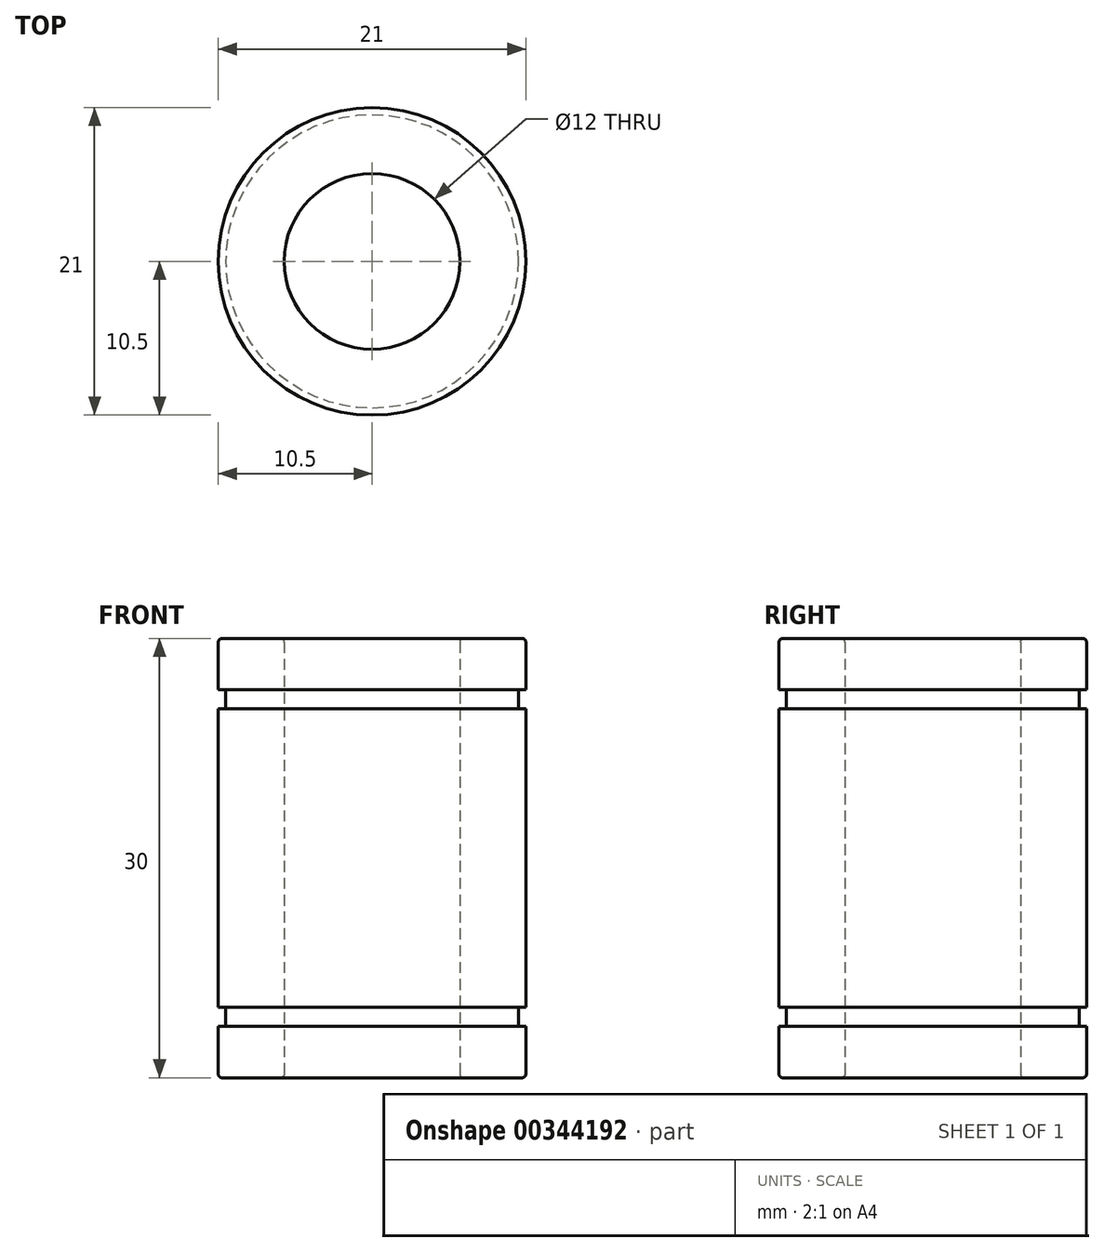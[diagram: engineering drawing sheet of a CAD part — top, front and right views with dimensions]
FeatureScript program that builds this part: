
annotation { "Feature Type Name" : "Feature", "Feature Type Description" : "" }
export const myFeature = defineFeature(function(context is Context, id is Id, definition is map)
    precondition{}
    {
        {
            var Q0;
            Q0=qCreatedBy(makeId("Top.planeOp"),FACE);
            var sketch = newSketch(context, id + "F0", { "sketchPlane" : qUnion([Q0])});
            skCircle(sketch, "E0", {"center": v(0, 0) * mm, "radius": 6 * mm});
            skCircle(sketch, "E1", {"center": v(0, 0) * mm, "radius": 10.5 * mm});
            skSolve(sketch);
        }
        {
            var Q0;
            Q0=qSketchRegion(id+"F0",true);
            extrude(context, id + "F1", {"entities" : qUnion([Q0]), "depth" : 30 * mm});
        }
        {
            var Q0;
            Q0=makeQuery(id+"F1.opExtrude","CAP_FACE",FACE,{"disambiguationData":[OSD([sQuery(id+"F0.wireOp",EDGE,"E0"),sQuery(id+"F0.wireOp",EDGE,"E1")])],"isStart":false});
            var Q1;
            Q1=makeQuery(id+"F1.opExtrude","CAP_FACE",FACE,{"disambiguationData":[OSD([sQuery(id+"F0.wireOp",EDGE,"E0"),sQuery(id+"F0.wireOp",EDGE,"E1")])],"isStart":true});
            fillet(context, id + "F2", {"entities" : qUnion([Q0, Q1]), "radius" : .25 * mm, "tangentPropagation" : true, "allowEdgeOverflow" : false});
        }
        {
            var Q0;
            Q0=makeQuery(id+"F1.opExtrude","CAP_FACE",FACE,{"disambiguationData":[OSD([sQuery(id+"F0.wireOp",EDGE,"E0"),sQuery(id+"F0.wireOp",EDGE,"E1")])],"isStart":false});
            var sketch = newSketch(context, id + "F3", { "sketchPlane" : qUnion([Q0])});
            skCircle(sketch, "E2", {"center": v(0, 0) * mm, "radius": 10 * mm});
            skCircle(sketch, "E3", {"center": v(0, 0) * mm, "radius": 16 * mm});
            skSolve(sketch);
        }
        {
            var Q0;
            Q0 = qSketchRegion(id + "F3", true);
            extrude(context, id + "F4", {"entities" : qUnion([Q0]), "operationType" : NewBodyOperationType.REMOVE, "oppositeDirection" : true, "depth" : 4.8 * mm, "hasSecondDirection" : true, "secondDirectionOppositeDirection" : true, "secondDirectionDepth" : 3.5 * mm});
        }
        {
            var Q0;
            Q0 = qSketchRegion(id + "F3", true);
            extrude(context, id + "F5", {"entities" : qUnion([Q0]), "operationType" : NewBodyOperationType.REMOVE, "oppositeDirection" : true, "depth" : 26.5 * mm, "hasSecondDirection" : true, "secondDirectionOppositeDirection" : true, "secondDirectionDepth" : 25.2 * mm});
        }
    });
